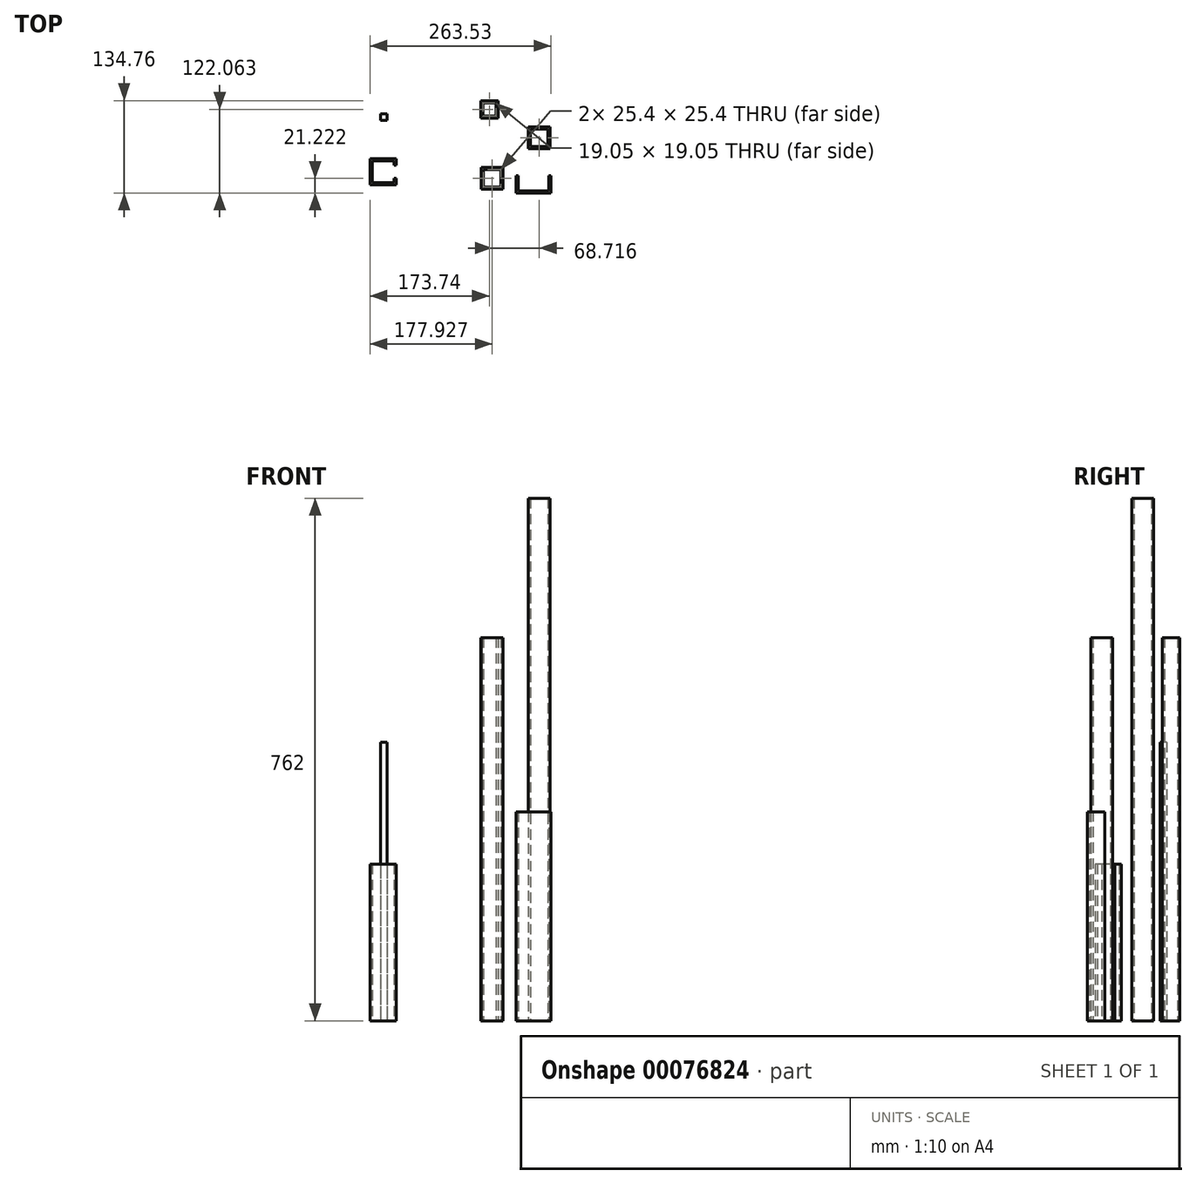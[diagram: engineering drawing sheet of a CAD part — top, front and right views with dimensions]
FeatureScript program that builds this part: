
annotation { "Feature Type Name" : "Feature", "Feature Type Description" : "" }
export const myFeature = defineFeature(function(context is Context, id is Id, definition is map)
    precondition{}
    {
        {
            var Q0;
            Q0=qCreatedBy(makeId("Top.planeOp"),FACE);
            var sketch = newSketch(context, id + "F0", { "sketchPlane" : qUnion([Q0])});
            skLineSegment(sketch, "E0.bottom", {"start": v(213.47, 53.37) * mm, "end": v(188.07, 53.37) * mm});
            skLineSegment(sketch, "E0.top", {"start": v(213.47, 78.77) * mm, "end": v(188.07, 78.77) * mm});
            skLineSegment(sketch, "E0.left", {"start": v(213.47, 53.37) * mm, "end": v(213.47, 78.77) * mm});
            skLineSegment(sketch, "E0.right", {"start": v(188.07, 53.37) * mm, "end": v(188.07, 78.77) * mm});
            skLineSegment(sketch, "E1", {"start": v(191.25, 75.6) * mm, "end": v(191.25, 56.55) * mm});
            skLineSegment(sketch, "E2", {"start": v(191.25, 56.55) * mm, "end": v(210.3, 56.55) * mm});
            skLineSegment(sketch, "E3", {"start": v(210.3, 56.55) * mm, "end": v(210.3, 75.6) * mm});
            skLineSegment(sketch, "E4", {"start": v(210.3, 75.6) * mm, "end": v(191.25, 75.6) * mm});
            skLineSegment(sketch, "E5", {"start": v(-316.83, 224.96) * mm, "end": v(-316.83, -177.73) * mm, "construction": true});
            skLineSegment(sketch, "E6", {"start": v(-428.8, -56.05) * mm, "end": v(404.55, -56.05) * mm, "construction": true});
            skLineSegment(sketch, "E7", {"start": v(-392.36, 42.38) * mm, "end": v(404.58, 42.38) * mm, "construction": true});
            skLineSegment(sketch, "E8", {"start": v(289.6, 224.86) * mm, "end": v(289.6, -143.53) * mm, "construction": true});
            skLineSegment(sketch, "E9.bottom", {"start": v(220.83, -50.64) * mm, "end": v(189.08, -50.64) * mm});
            skLineSegment(sketch, "E9.top", {"start": v(220.83, -18.9) * mm, "end": v(189.08, -18.9) * mm});
            skLineSegment(sketch, "E9.left", {"start": v(220.83, -50.64) * mm, "end": v(220.83, -18.9) * mm});
            skLineSegment(sketch, "E9.right", {"start": v(189.08, -50.64) * mm, "end": v(189.08, -18.9) * mm});
            skLineSegment(sketch, "E10", {"start": v(192.26, -22.07) * mm, "end": v(192.26, -47.47) * mm});
            skLineSegment(sketch, "E11", {"start": v(192.26, -47.47) * mm, "end": v(217.66, -47.47) * mm});
            skLineSegment(sketch, "E12", {"start": v(217.66, -47.47) * mm, "end": v(217.66, -22.07) * mm});
            skLineSegment(sketch, "E13", {"start": v(217.66, -22.07) * mm, "end": v(192.26, -22.07) * mm});
            skLineSegment(sketch, "E14", {"start": v(290.56, -30.6) * mm, "end": v(290.56, -56) * mm});
            skLineSegment(sketch, "E15", {"start": v(290.56, -56) * mm, "end": v(239.76, -56) * mm});
            skLineSegment(sketch, "E16", {"start": v(239.76, -56) * mm, "end": v(239.76, -30.6) * mm});
            skLineSegment(sketch, "E17", {"start": v(239.76, -30.6) * mm, "end": v(243.19, -30.6) * mm});
            skLineSegment(sketch, "E18", {"start": v(243.19, -30.6) * mm, "end": v(243.19, -52.69) * mm});
            skLineSegment(sketch, "E19", {"start": v(243.19, -52.69) * mm, "end": v(287.26, -52.69) * mm});
            skLineSegment(sketch, "E20", {"start": v(287.26, -52.69) * mm, "end": v(287.26, -30.6) * mm});
            skLineSegment(sketch, "E21", {"start": v(287.26, -30.6) * mm, "end": v(290.56, -30.6) * mm});
            skLineSegment(sketch, "E22.bottom", {"start": v(289.6, 40.66) * mm, "end": v(257.85, 40.66) * mm});
            skLineSegment(sketch, "E22.top", {"start": v(289.6, 8.91) * mm, "end": v(257.85, 8.91) * mm});
            skLineSegment(sketch, "E22.left", {"start": v(289.6, 40.66) * mm, "end": v(289.6, 8.91) * mm});
            skLineSegment(sketch, "E22.right", {"start": v(257.85, 40.66) * mm, "end": v(257.85, 8.91) * mm});
            skLineSegment(sketch, "E23.bottom", {"start": v(260.97, 37.49) * mm, "end": v(286.37, 37.49) * mm});
            skLineSegment(sketch, "E23.top", {"start": v(260.97, 12.09) * mm, "end": v(286.37, 12.09) * mm});
            skLineSegment(sketch, "E23.left", {"start": v(260.97, 37.49) * mm, "end": v(260.97, 12.09) * mm});
            skLineSegment(sketch, "E23.right", {"start": v(286.37, 37.49) * mm, "end": v(286.37, 12.09) * mm});
            skLineSegment(sketch, "E24.bottom", {"start": v(65.13, -5.96) * mm, "end": v(27.03, -5.96) * mm});
            skLineSegment(sketch, "E24.top", {"start": v(65.13, -44.06) * mm, "end": v(27.03, -44.06) * mm});
            skLineSegment(sketch, "E24.left", {"start": v(65.13, -5.96) * mm, "end": v(65.13, -44.06) * mm});
            skLineSegment(sketch, "E24.right", {"start": v(27.03, -5.96) * mm, "end": v(27.03, -44.06) * mm});
            skLineSegment(sketch, "E25.bottom", {"start": v(30.2, -9.13) * mm, "end": v(61.96, -9.13) * mm});
            skLineSegment(sketch, "E25.top", {"start": v(30.2, -40.88) * mm, "end": v(61.96, -40.88) * mm});
            skLineSegment(sketch, "E25.left", {"start": v(30.2, -9.13) * mm, "end": v(30.2, -40.88) * mm});
            skLineSegment(sketch, "E25.right", {"start": v(61.96, -9.13) * mm, "end": v(61.96, -40.88) * mm});
            skLineSegment(sketch, "E26.bottom", {"start": v(42.13, 59.51) * mm, "end": v(51.65, 59.51) * mm});
            skLineSegment(sketch, "E26.top", {"start": v(42.13, 49.99) * mm, "end": v(51.65, 49.99) * mm});
            skLineSegment(sketch, "E26.left", {"start": v(42.13, 59.51) * mm, "end": v(42.13, 49.99) * mm});
            skLineSegment(sketch, "E26.right", {"start": v(51.65, 59.51) * mm, "end": v(51.65, 49.99) * mm});
            skLineSegment(sketch, "E27", {"start": v(61.96, -15.48) * mm, "end": v(65.13, -15.48) * mm});
            skLineSegment(sketch, "E28", {"start": v(61.96, -34.53) * mm, "end": v(65.13, -34.53) * mm});
            skSolve(sketch);
        }
        {
            var Q0;
            Q0=makeQuery(id+"F0.imprint","IMPRINT",FACE,{"disambiguationData":[TD([[makeQuery(id+"F0.imprint","IMPRINT",EDGE,{"derivedFrom":sQuery(id+"F0.wireOp",EDGE,"E0.bottom")}),-1.0]])]});
            extrude(context, id + "F1", {"entities" : qUnion([Q0]), "depth" : 558.8 * mm});
        }
        {
            var Q0;
            Q0=makeQuery(id+"F0.imprint","IMPRINT",FACE,{"disambiguationData":[TD([[makeQuery(id+"F0.imprint","IMPRINT",EDGE,{"derivedFrom":sQuery(id+"F0.wireOp",EDGE,"E9.bottom")}),-1.0]])]});
            extrude(context, id + "F2", {"entities" : qUnion([Q0]), "depth" : 558.8 * mm});
        }
        {
            var Q0;
            Q0=makeQuery(id+"F0.imprint","IMPRINT",FACE,{"disambiguationData":[TD([[makeQuery(id+"F0.imprint","IMPRINT",EDGE,{"derivedFrom":sQuery(id+"F0.wireOp",EDGE,"E22.bottom")}),1.0]])]});
            extrude(context, id + "F3", {"entities" : qUnion([Q0]), "depth" : 762 * mm});
        }
        {
            var Q0;
            Q0=makeQuery(id+"F0.imprint","IMPRINT",FACE,{"disambiguationData":[TD([[makeQuery(id+"F0.imprint","IMPRINT",EDGE,{"derivedFrom":sQuery(id+"F0.wireOp",EDGE,"E24.bottom")}),1.0]])]});
            extrude(context, id + "F4", {"entities" : qUnion([Q0]), "depth" : 228.6 * mm});
        }
        {
            var Q0;
            Q0=makeQuery(id+"F0.imprint","IMPRINT",FACE,{"disambiguationData":[TD([[makeQuery(id+"F0.imprint","IMPRINT",EDGE,{"derivedFrom":sQuery(id+"F0.wireOp",EDGE,"E14")}),-1.0]])]});
            extrude(context, id + "F5", {"entities" : qUnion([Q0]), "depth" : 304.8 * mm});
        }
        {
            var Q0;
            Q0=makeQuery(id+"F0.imprint","IMPRINT",FACE,{"disambiguationData":[TD([[makeQuery(id+"F0.imprint","IMPRINT",EDGE,{"derivedFrom":sQuery(id+"F0.wireOp",EDGE,"E26.bottom")}),-1.0]])]});
            extrude(context, id + "F6", {"entities" : qUnion([Q0]), "depth" : 406.4 * mm});
        }
    });
